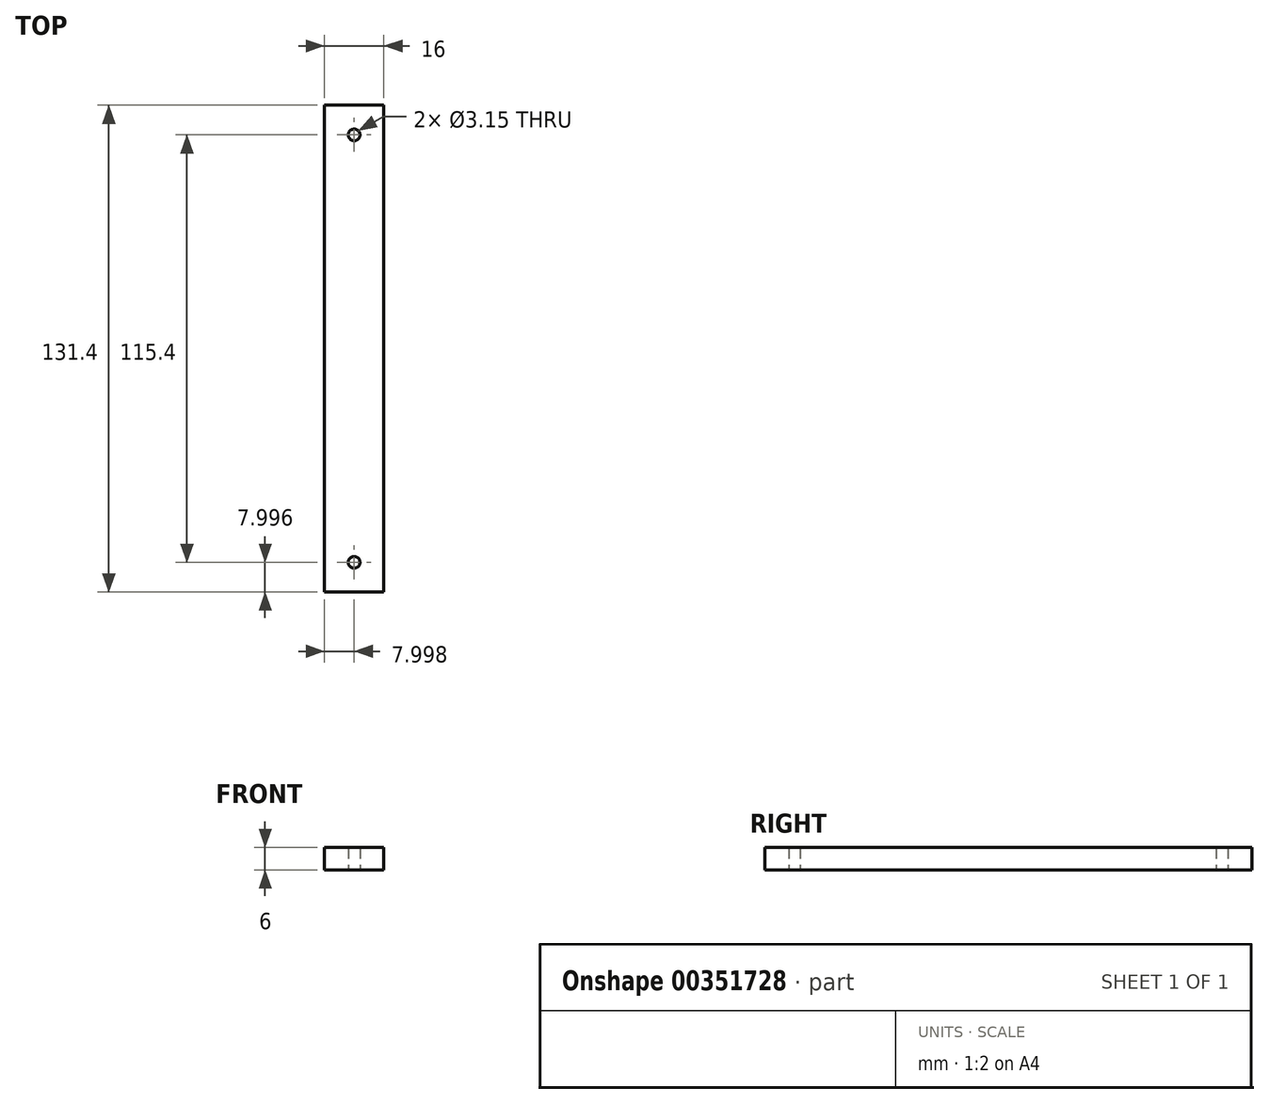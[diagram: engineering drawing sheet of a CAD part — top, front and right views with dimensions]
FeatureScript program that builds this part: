
annotation { "Feature Type Name" : "Feature", "Feature Type Description" : "" }
export const myFeature = defineFeature(function(context is Context, id is Id, definition is map)
    precondition{}
    {
        {
            var Q0;
            Q0=qCreatedBy(makeId("Top.planeOp"),FACE);
            var sketch = newSketch(context, id + "F0", { "sketchPlane" : qUnion([Q0])});
            skLineSegment(sketch, "E0.bottom", {"start": v(-594.2, 88.73) * mm, "end": v(-578.2, 88.73) * mm});
            skLineSegment(sketch, "E0.top", {"start": v(-594.2, -42.67) * mm, "end": v(-578.2, -42.67) * mm});
            skLineSegment(sketch, "E0.left", {"start": v(-594.2, 88.73) * mm, "end": v(-594.2, -42.67) * mm});
            skLineSegment(sketch, "E0.right", {"start": v(-578.2, 88.73) * mm, "end": v(-578.2, -42.67) * mm});
            skCircle(sketch, "E1", {"center": v(-586.2, 80.73) * mm, "radius": 1.57 * mm});
            skCircle(sketch, "E2", {"center": v(68.82, 80.73) * mm, "radius": 1.57 * mm});
            skCircle(sketch, "E3", {"center": v(68.82, -34.67) * mm, "radius": 1.57 * mm});
            skCircle(sketch, "E4", {"center": v(-586.2, -34.67) * mm, "radius": 1.57 * mm});
            skLineSegment(sketch, "E5", {"start": v(-586.2, -34.67) * mm, "end": v(-586.2, 80.73) * mm, "construction": true});
            skSolve(sketch);
        }
        {
            var Q0;
            Q0=makeQuery(id+"F0.imprint","IMPRINT",FACE,{"disambiguationData":[TD([[makeQuery(id+"F0.imprint","IMPRINT",EDGE,{"derivedFrom":sQuery(id+"F0.wireOp",EDGE,"E0.bottom")}),-1.0]])]});
            extrude(context, id + "F1", {"entities" : qUnion([Q0]), "depth" : 6 * mm});
        }
    });
